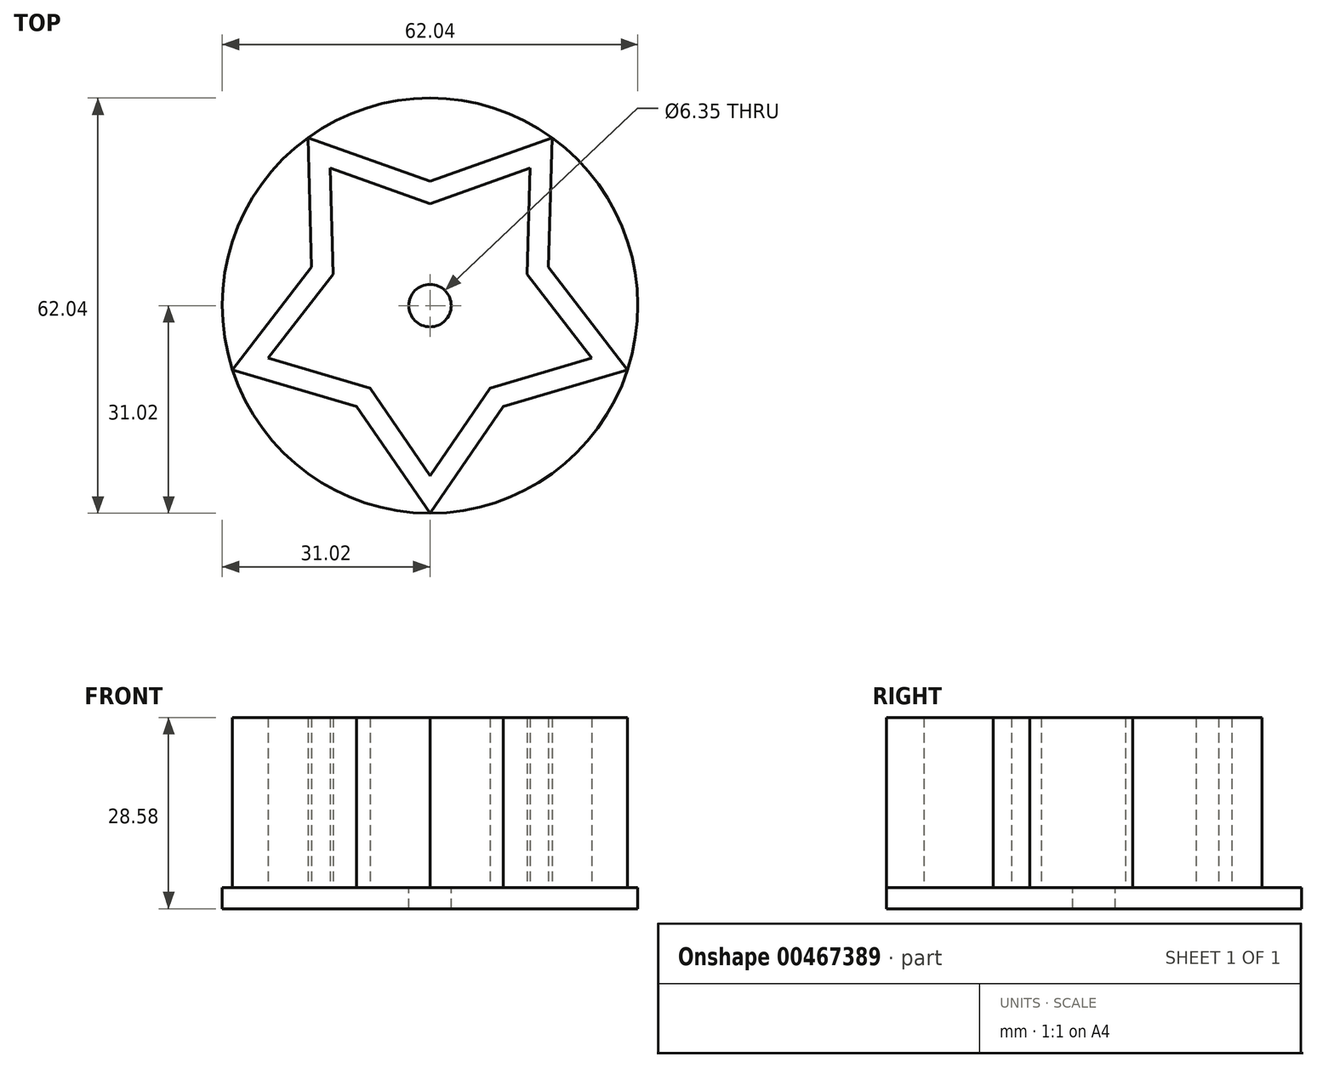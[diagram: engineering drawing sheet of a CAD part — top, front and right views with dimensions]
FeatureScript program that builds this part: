
annotation { "Feature Type Name" : "Feature", "Feature Type Description" : "" }
export const myFeature = defineFeature(function(context is Context, id is Id, definition is map)
    precondition{}
    {
        {
            var Q0;
            Q0=qCreatedBy(makeId("Top.planeOp"),FACE);
            var sketch = newSketch(context, id + "F0", { "sketchPlane" : qUnion([Q0])});
            skCircle(sketch, "E0", {"center": v(0, 0) * mm, "radius": 25.4 * mm, "construction": true});
            skPoint(sketch, "E1", {"position": v(0, -25.4) * mm});
            skPoint(sketch, "E2.1.0", {"position": v(24.16, -7.85) * mm});
            skPoint(sketch, "E2.2.0", {"position": v(14.93, 20.55) * mm});
            skPoint(sketch, "E2.3.0", {"position": v(-14.93, 20.55) * mm});
            skPoint(sketch, "E2.4.0", {"position": v(-24.16, -7.85) * mm});
            skLineSegment(sketch, "E3", {"start": v(0, 0) * mm, "end": v(-28.06, -38.62) * mm, "construction": true});
            skPoint(sketch, "E4", {"position": v(-8.96, -12.33) * mm});
            skPoint(sketch, "E5.1.0", {"position": v(8.96, -12.33) * mm});
            skPoint(sketch, "E5.2.0", {"position": v(14.5, 4.7) * mm});
            skPoint(sketch, "E5.3.0", {"position": v(0, 15.24) * mm});
            skPoint(sketch, "E5.4.0", {"position": v(-14.5, 4.7) * mm});
            skLineSegment(sketch, "E6", {"start": v(0, -25.4) * mm, "end": v(-8.96, -12.33) * mm});
            skLineSegment(sketch, "E7", {"start": v(-8.96, -12.33) * mm, "end": v(-24.16, -7.85) * mm});
            skLineSegment(sketch, "E8", {"start": v(-24.16, -7.85) * mm, "end": v(-14.5, 4.7) * mm});
            skLineSegment(sketch, "E9", {"start": v(-14.5, 4.7) * mm, "end": v(-14.93, 20.55) * mm});
            skLineSegment(sketch, "E10", {"start": v(-14.93, 20.55) * mm, "end": v(0, 15.24) * mm});
            skLineSegment(sketch, "E11", {"start": v(0, 15.24) * mm, "end": v(14.93, 20.55) * mm});
            skLineSegment(sketch, "E12", {"start": v(14.93, 20.55) * mm, "end": v(14.5, 4.7) * mm});
            skLineSegment(sketch, "E13", {"start": v(14.5, 4.7) * mm, "end": v(24.16, -7.85) * mm});
            skLineSegment(sketch, "E14", {"start": v(24.16, -7.85) * mm, "end": v(8.96, -12.33) * mm});
            skLineSegment(sketch, "E15", {"start": v(8.96, -12.33) * mm, "end": v(0, -25.4) * mm});
            skLineSegment(sketch, "E16.0", {"start": v(17.7, 5.75) * mm, "end": v(29.5, -9.58) * mm});
            skLineSegment(sketch, "E16.1", {"start": v(18.23, 25.1) * mm, "end": v(17.7, 5.75) * mm});
            skLineSegment(sketch, "E16.2", {"start": v(29.5, -9.58) * mm, "end": v(10.94, -15.06) * mm});
            skLineSegment(sketch, "E16.3", {"start": v(0, 18.6) * mm, "end": v(18.23, 25.1) * mm});
            skLineSegment(sketch, "E16.4", {"start": v(-18.23, 25.1) * mm, "end": v(0, 18.6) * mm});
            skLineSegment(sketch, "E16.5", {"start": v(-17.7, 5.75) * mm, "end": v(-18.23, 25.1) * mm});
            skLineSegment(sketch, "E16.6", {"start": v(10.94, -15.06) * mm, "end": v(0, -31.02) * mm});
            skLineSegment(sketch, "E16.7", {"start": v(0, -31.02) * mm, "end": v(-10.94, -15.06) * mm});
            skLineSegment(sketch, "E16.8", {"start": v(-10.94, -15.06) * mm, "end": v(-29.5, -9.58) * mm});
            skLineSegment(sketch, "E16.9", {"start": v(-29.5, -9.58) * mm, "end": v(-17.7, 5.75) * mm});
            skSolve(sketch);
        }
        {
            var Q0;
            Q0=makeQuery(id+"F0.imprint","IMPRINT",FACE,{"disambiguationData":[TD([[makeQuery(id+"F0.imprint","IMPRINT",EDGE,{"derivedFrom":sQuery(id+"F0.wireOp",EDGE,"E6")}),1.0]])]});
            extrude(context, id + "F1", {"entities" : qUnion([Q0]), "depth" : 25.4 * mm});
        }
        {
            var Q0;
            Q0=makeQuery(id+"F1.opExtrude","CAP_FACE",FACE,{"disambiguationData":[OSD([sQuery(id+"F0.wireOp",EDGE,"E6"),sQuery(id+"F0.wireOp",EDGE,"E7"),sQuery(id+"F0.wireOp",EDGE,"E8"),sQuery(id+"F0.wireOp",EDGE,"E9"),sQuery(id+"F0.wireOp",EDGE,"E10"),sQuery(id+"F0.wireOp",EDGE,"E11"),sQuery(id+"F0.wireOp",EDGE,"E12"),sQuery(id+"F0.wireOp",EDGE,"E13"),sQuery(id+"F0.wireOp",EDGE,"E14"),sQuery(id+"F0.wireOp",EDGE,"E15"),sQuery(id+"F0.wireOp",EDGE,"E16.0"),sQuery(id+"F0.wireOp",EDGE,"E16.1"),sQuery(id+"F0.wireOp",EDGE,"E16.2"),sQuery(id+"F0.wireOp",EDGE,"E16.3"),sQuery(id+"F0.wireOp",EDGE,"E16.4"),sQuery(id+"F0.wireOp",EDGE,"E16.5"),sQuery(id+"F0.wireOp",EDGE,"E16.6"),sQuery(id+"F0.wireOp",EDGE,"E16.7"),sQuery(id+"F0.wireOp",EDGE,"E16.8"),sQuery(id+"F0.wireOp",EDGE,"E16.9")])],"isStart":true});
            var sketch = newSketch(context, id + "F2", { "sketchPlane" : qUnion([Q0])});
            skCircle(sketch, "E17", {"center": v(0, 0) * mm, "radius": 31.02 * mm});
            skCircle(sketch, "E18", {"center": v(0, 0) * mm, "radius": 3.18 * mm});
            skSolve(sketch);
        }
        {
            var Q0;
            Q0 = qSketchRegion(id + "F2", true);
            extrude(context, id + "F3", {"entities" : qUnion([Q0]), "operationType" : NewBodyOperationType.ADD, "depth" : 3.17 * mm});
        }
    });
